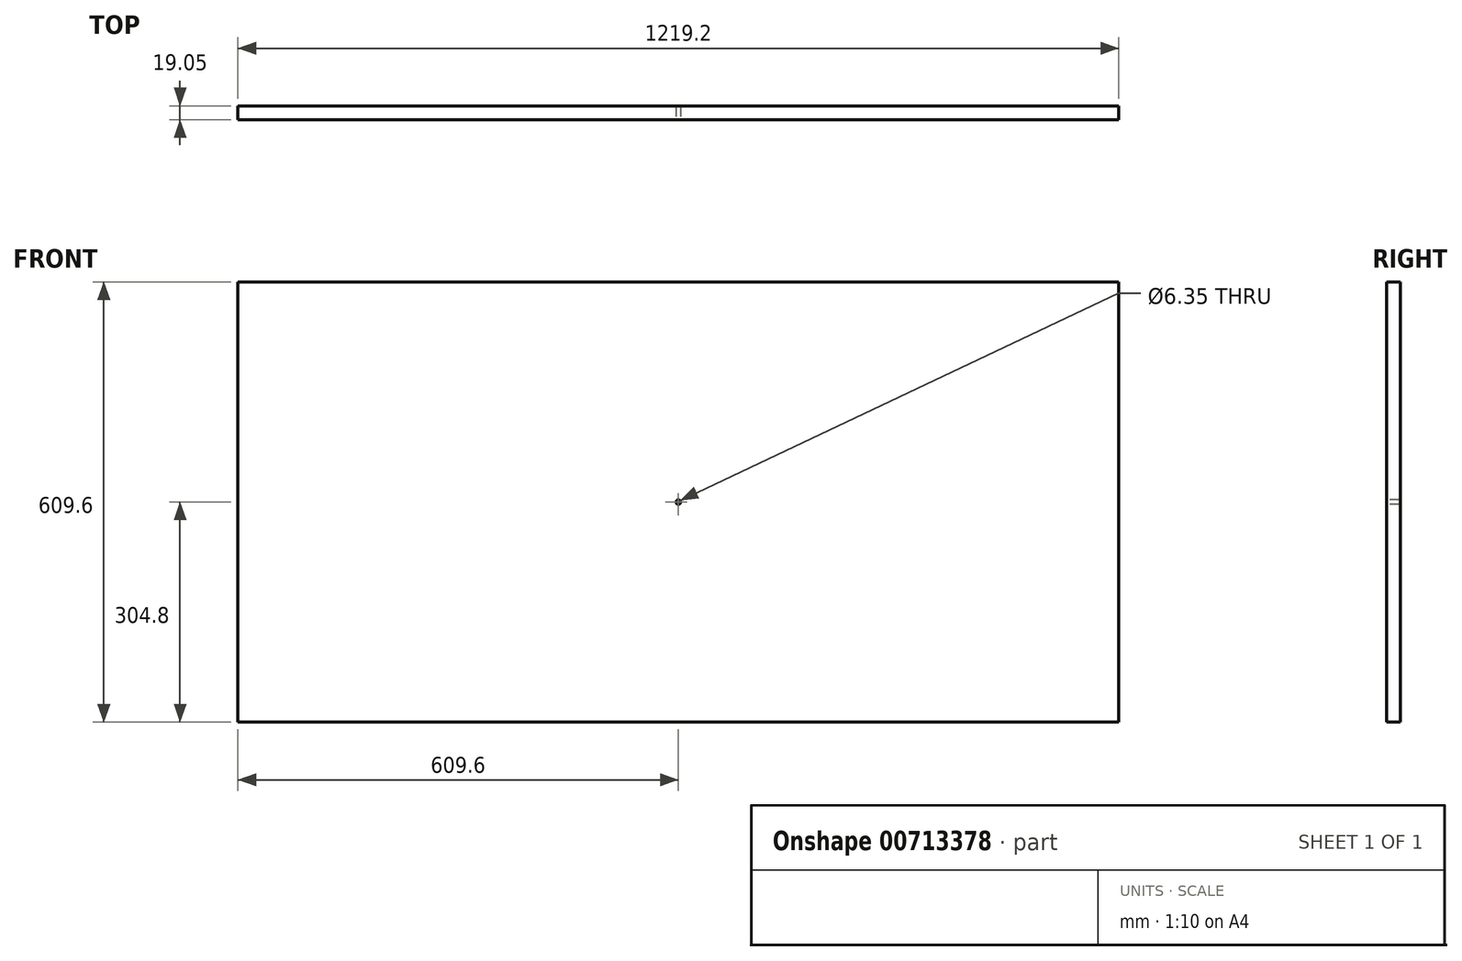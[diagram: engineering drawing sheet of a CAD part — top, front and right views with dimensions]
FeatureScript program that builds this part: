
annotation { "Feature Type Name" : "Feature", "Feature Type Description" : "" }
export const myFeature = defineFeature(function(context is Context, id is Id, definition is map)
    precondition{}
    {
        {
            var Q0;
            Q0=qCreatedBy(makeId("Front.planeOp"),FACE);
            var sketch = newSketch(context, id + "F0", { "sketchPlane" : qUnion([Q0])});
            skLineSegment(sketch, "E0.bottom", {"start": v(0, 0) * mm, "end": v(-1219.2, 0) * mm});
            skLineSegment(sketch, "E0.top", {"start": v(0, 609.6) * mm, "end": v(-1219.2, 609.6) * mm});
            skLineSegment(sketch, "E0.left", {"start": v(0, 0) * mm, "end": v(0, 609.6) * mm});
            skLineSegment(sketch, "E0.right", {"start": v(-1219.2, 0) * mm, "end": v(-1219.2, 609.6) * mm});
            skSolve(sketch);
        }
        {
            var Q0;
            Q0=makeQuery(id+"F0.imprint","IMPRINT",FACE,{"disambiguationData":[TD([[makeQuery(id+"F0.imprint","IMPRINT",EDGE,{"derivedFrom":sQuery(id+"F0.wireOp",EDGE,"E0.bottom")}),-1.0]])]});
            extrude(context, id + "F1", {"entities" : qUnion([Q0]), "depth" : 19.05 * mm, "offsetDistance" : 25.4 * mm});
        }
        {
            var Q0;
            Q0=makeQuery(id+"F1.opExtrude","CAP_FACE",FACE,{"disambiguationData":[OSD([sQuery(id+"F0.wireOp",EDGE,"E0.bottom"),sQuery(id+"F0.wireOp",EDGE,"E0.top"),sQuery(id+"F0.wireOp",EDGE,"E0.left"),sQuery(id+"F0.wireOp",EDGE,"E0.right")])],"isStart":false});
            var sketch = newSketch(context, id + "F2", { "sketchPlane" : qUnion([Q0])});
            skLineSegment(sketch, "E1", {"start": v(-1219.2, 304.8) * mm, "end": v(-609.6, 304.8) * mm, "construction": true});
            skLineSegment(sketch, "E2", {"start": v(-609.6, 304.8) * mm, "end": v(-609.6, 609.6) * mm, "construction": true});
            skCircle(sketch, "E3", {"center": v(-609.6, 304.8) * mm, "radius": 3.17 * mm});
            skSolve(sketch);
        }
        {
            var Q0;
            Q0 = qSketchRegion(id + "F2", true);
            extrude(context, id + "F3", {"entities" : qUnion([Q0]), "operationType" : NewBodyOperationType.REMOVE, "oppositeDirection" : true, "depth" : 25.4 * mm, "offsetDistance" : 25.4 * mm});
        }
    });
